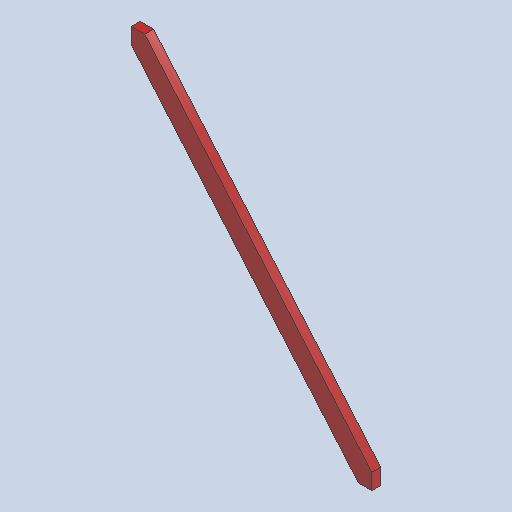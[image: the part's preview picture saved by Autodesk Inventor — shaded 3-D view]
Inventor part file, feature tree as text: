
AUTODESK INVENTOR PART (.ipt)
format: ipt  version: 2025 (Build 290162000, 162)  size: 92,160 bytes
history: native  units: in
note: dims shown in document units (in); Inventor stores cm internally (conversion verified against a paired STEP export)
features: other x7, reference x4, extrude x1, sketch x1
ambient origin geometry x8: Origin, YZ Plane, XZ Plane, XY Plane, X Axis, Y Axis, Z Axis, Center Point
bodies: Solid1 (feature_tree)
feature tree (13):
  extrude  "Extrusion1"  [1 undecoded]
  sketch  "Sketch1"  dims[d2=1.5in d3=0.0in]
  reference  "Reference1"
  reference  "Reference2"
  reference  "Reference3"
  reference  "Reference4"
  other  "<userpath>\Documents\Tburn24\B_Legs0\B_Legs0.iam"
  other  "B_Legs0.iam"
  other  "4x2x4:1"
  other  "3'5x2x4:1"
  other  "4x2x4:2"
  other  "3'5x2x4:4"
  other  "Finish1"
note: 1 required parameter value undecoded (feature->parameter linkage not recoverable at this tier; creation-order binding heuristic only, values carry confidence <= 0.55)
